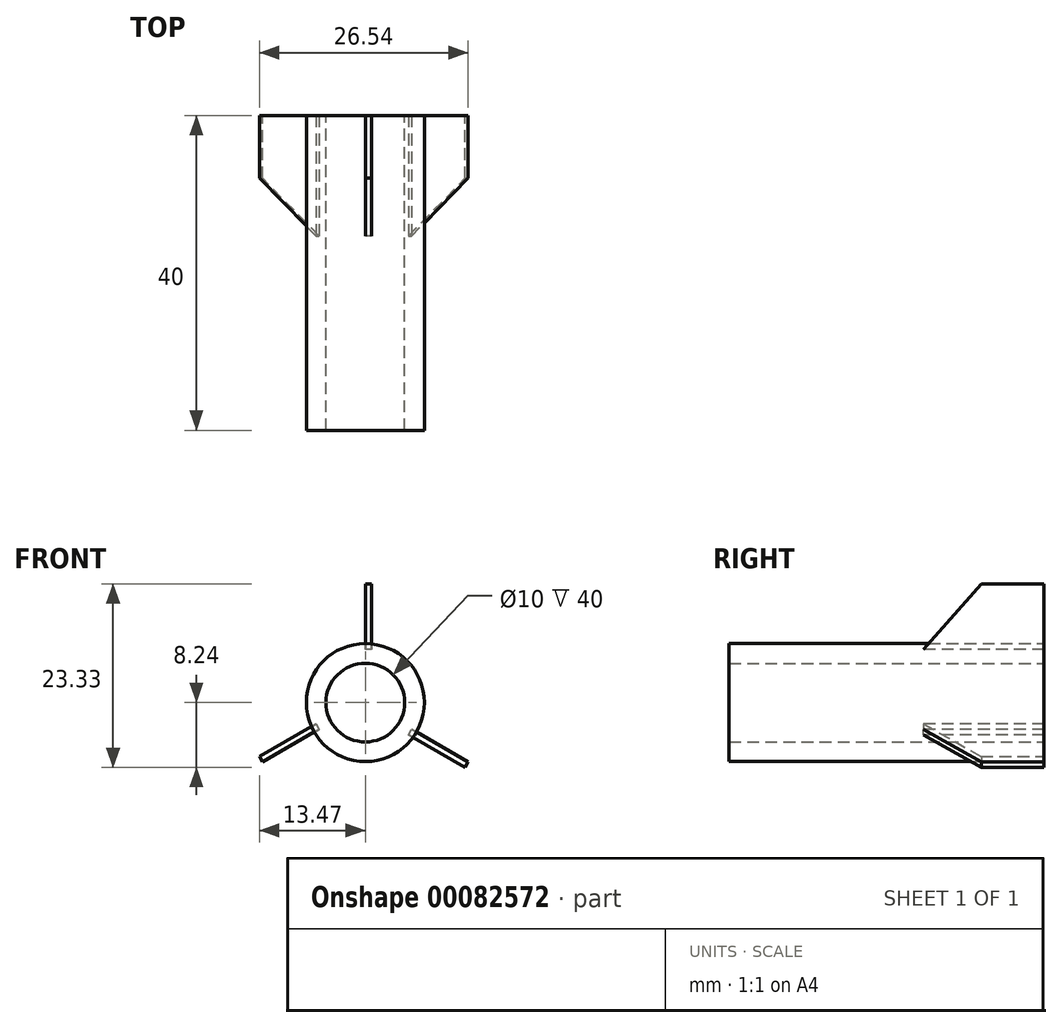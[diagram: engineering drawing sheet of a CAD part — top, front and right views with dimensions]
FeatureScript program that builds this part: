
annotation { "Feature Type Name" : "Feature", "Feature Type Description" : "" }
export const myFeature = defineFeature(function(context is Context, id is Id, definition is map)
    precondition{}
    {
        {
            var Q0;
            Q0=qCreatedBy(makeId("Front.planeOp"),FACE);
            var sketch = newSketch(context, id + "F0", { "sketchPlane" : qUnion([Q0])});
            skCircle(sketch, "E0", {"center": v(0, 0) * mm, "radius": 5 * mm});
            skCircle(sketch, "E1", {"center": v(0, 0) * mm, "radius": 7.5 * mm});
            skSolve(sketch);
        }
        {
            var Q0;
            Q0=makeQuery(id+"F0.imprint","IMPRINT",FACE,{"disambiguationData":[TD([[makeQuery(id+"F0.imprint","IMPRINT",EDGE,{"derivedFrom":sQuery(id+"F0.wireOp",EDGE,"E0")}),-1.0]])]});
            extrude(context, id + "F1", {"entities" : qUnion([Q0]), "depth" : 40 * mm});
        }
        {
            var Q0;
            Q0=qCreatedBy(makeId("Right.planeOp"),FACE);
            var sketch = newSketch(context, id + "F2", { "sketchPlane" : qUnion([Q0])});
            skLineSegment(sketch, "E2", {"start": v(0, 6.77) * mm, "end": v(-15.34, 6.77) * mm});
            skLineSegment(sketch, "E3", {"start": v(-15.34, 6.77) * mm, "end": v(-7.97, 15.1) * mm});
            skLineSegment(sketch, "E4", {"start": v(-7.97, 15.1) * mm, "end": v(0, 15.1) * mm});
            skLineSegment(sketch, "E5", {"start": v(0, 15.1) * mm, "end": v(0, 6.77) * mm});
            skSolve(sketch);
        }
        {
            var Q0;
            Q0=makeQuery(id+"F2.imprint","IMPRINT",FACE,{"disambiguationData":[TD([[makeQuery(id+"F2.imprint","IMPRINT",EDGE,{"derivedFrom":sQuery(id+"F2.wireOp",EDGE,"E2")}),-1.0]])]});
            extrude(context, id + "F3", {"entities" : qUnion([Q0]), "depth" : 0.8 * mm});
        }
        {
            var Q0;
            Q0=makeQuery(id+"F3.opExtrude","SWEPT_BODY",BODY,{"disambiguationData":[OSD([sQuery(id+"F2.wireOp",EDGE,"E2"),sQuery(id+"F2.wireOp",EDGE,"E3"),sQuery(id+"F2.wireOp",EDGE,"E4"),sQuery(id+"F2.wireOp",EDGE,"E5")])]});
            var Q1;
            Q1=makeQuery(id+"F1.opExtrude","SWEPT_FACE",FACE,{"disambiguationData":[OSD([sQuery(id+"F0.wireOp",EDGE,"E1")])]});
            circularPattern(context, id + "F4", {"entities" : qUnion([Q0]), "axis" : qUnion([Q1]), "angle" : 360 * degree, "instanceCount" : 3, "equalSpace" : true});
        }
    });
